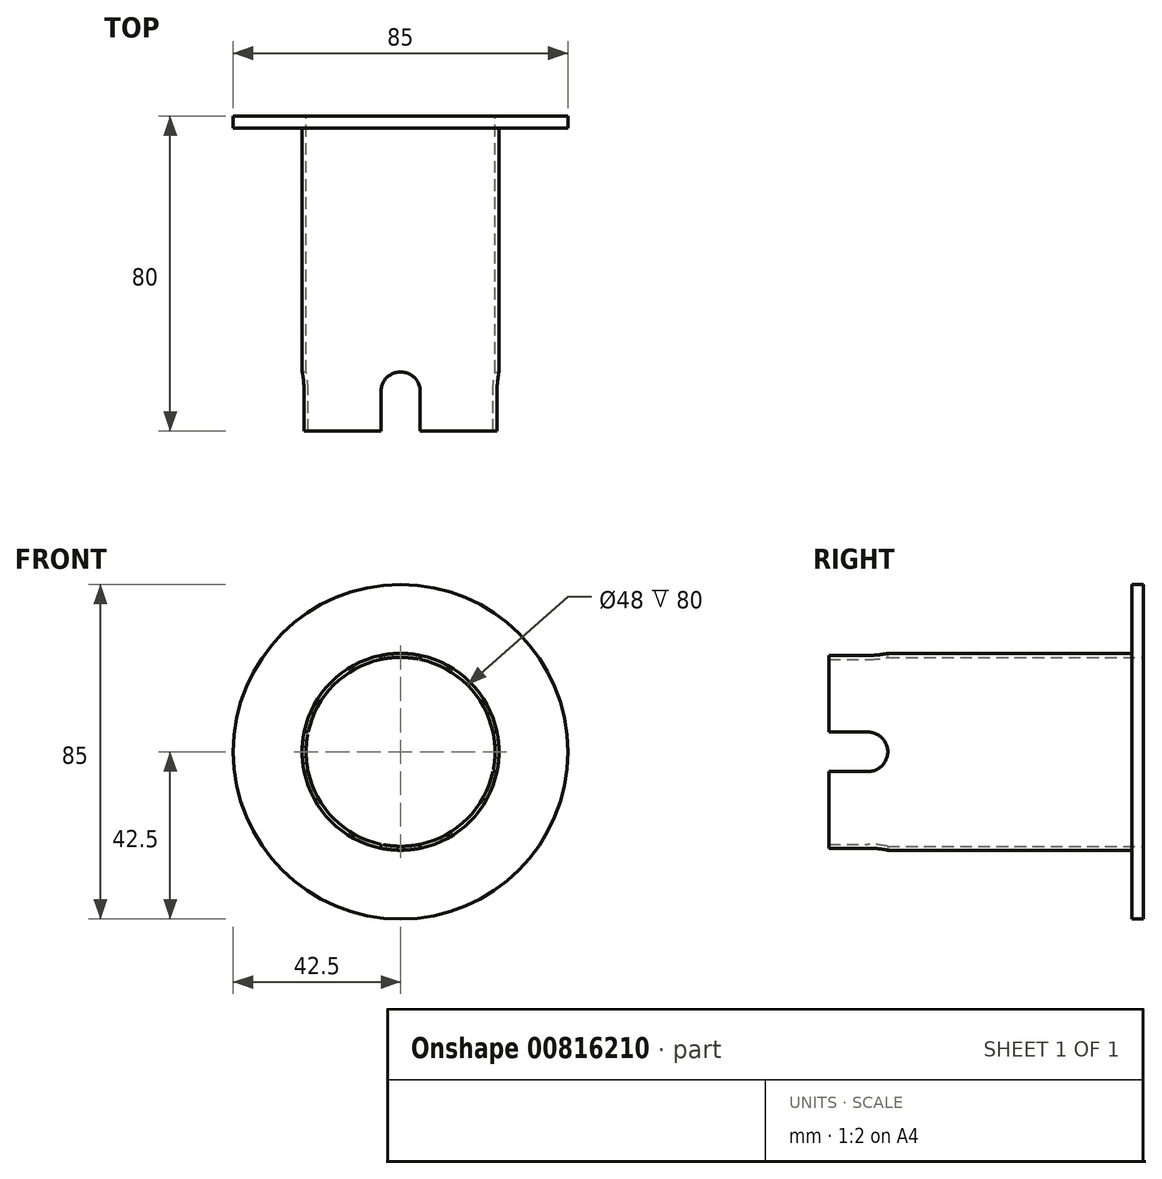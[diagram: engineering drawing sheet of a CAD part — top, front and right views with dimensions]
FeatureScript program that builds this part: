
annotation { "Feature Type Name" : "Feature", "Feature Type Description" : "" }
export const myFeature = defineFeature(function(context is Context, id is Id, definition is map)
    precondition{}
    {
        {
            var Q0;
            Q0=qCreatedBy(makeId("Front.planeOp"),FACE);
            var sketch = newSketch(context, id + "F0", { "sketchPlane" : qUnion([Q0])});
            skCircle(sketch, "E0", {"center": v(0, 0) * mm, "radius": 25 * mm});
            skCircle(sketch, "E1", {"center": v(0, 0) * mm, "radius": 42.5 * mm});
            skCircle(sketch, "E2", {"center": v(0, 0) * mm, "radius": 24 * mm});
            skSolve(sketch);
        }
        {
            var Q0;
            Q0=makeQuery(id+"F0.imprint","IMPRINT",FACE,{"disambiguationData":[TD([[makeQuery(id+"F0.imprint","IMPRINT",EDGE,{"derivedFrom":sQuery(id+"F0.wireOp",EDGE,"E1")}),1.0]])]});
            var Q1;
            Q1=makeQuery(id+"F0.imprint","IMPRINT",FACE,{"disambiguationData":[TD([[makeQuery(id+"F0.imprint","IMPRINT",EDGE,{"derivedFrom":sQuery(id+"F0.wireOp",EDGE,"E0")}),-1.0]])]});
            extrude(context, id + "F1", {"entities" : qUnion([Q0, Q1]), "depth" : 3 * mm, "offsetDistance" : 25 * mm});
        }
        {
            var Q0;
            Q0=qCreatedBy(makeId("Top.planeOp"),FACE);
            cPlane(context, id + "F2", {"entities" : qUnion([Q0]), "cplaneType" : CPlaneType.OFFSET, "offset" : 25 * mm, "width" : 150 * mm, "height" : 150 * mm});
        }
        {
            var Q0;
            Q0=makeQuery(id+"F0.imprint","IMPRINT",FACE,{"disambiguationData":[TD([[makeQuery(id+"F0.imprint","IMPRINT",EDGE,{"derivedFrom":sQuery(id+"F0.wireOp",EDGE,"E0")}),1.0]])]});
            extrude(context, id + "F3", {"entities" : qUnion([Q0]), "operationType" : NewBodyOperationType.ADD, "depth" : 80 * mm, "offsetDistance" : 25 * mm});
        }
        {
            var Q0;
            Q0=qCreatedBy(id+"F2.planeOp",FACE);
            var sketch = newSketch(context, id + "F4", { "sketchPlane" : qUnion([Q0])});
            skLineSegment(sketch, "E3.bottom", {"start": v(-5, -80) * mm, "end": v(5, -80) * mm});
            skLineSegment(sketch, "E3.top", {"start": v(0, -65) * mm, "end": v(0, -65) * mm});
            skLineSegment(sketch, "E3.left", {"start": v(-5, -80) * mm, "end": v(-5, -70) * mm});
            skLineSegment(sketch, "E3.right", {"start": v(5, -80) * mm, "end": v(5, -70) * mm});
            skLineSegment(sketch, "E4", {"start": v(0, -69.84) * mm, "end": v(0, -83.22) * mm, "construction": true});
            skPoint(sketch, "E5", {"position": v(0, -80) * mm});
            skLineSegment(sketch, "E6.0", {"start": v(25, -80) * mm, "end": v(-25, -80) * mm});
            skPoint(sketch, "E7.visualSharp", {"position": v(-5, -65) * mm});
            skArc(sketch, "E7.filletArc", {"start": v(0, -65) * mm, "mid": v(-3.54, -66.46) * mm, "end": v(-5, -70) * mm});
            skPoint(sketch, "E8.visualSharp", {"position": v(5, -65) * mm});
            skArc(sketch, "E8.filletArc", {"start": v(5, -70) * mm, "mid": v(3.54, -66.46) * mm, "end": v(0, -65) * mm});
            skSolve(sketch);
        }
        {
            var Q0;
            {var subQ1=sQuery(id+"F4.wireOp",EDGE,"E3.left");Q0=makeQuery(id+"F4.imprint","IMPRINT",FACE,{"disambiguationData":[TD([[makeQuery(id+"F4.imprint","IMPRINT",EDGE,{"derivedFrom":subQ1}),-1.0]])]});}
            extrude(context, id + "F5", {"entities" : qUnion([Q0]), "oppositeDirection" : true, "depth" : 2 * mm, "offsetDistance" : 25 * mm});
        }
        {
            var Q0;
            Q0=makeQuery(id+"F5.opExtrude","SWEPT_BODY",BODY,{"disambiguationData":[OSD([sQuery(id+"F4.wireOp",EDGE,"E3.left"),sQuery(id+"F4.wireOp",EDGE,"E3.right"),sQuery(id+"F4.wireOp",EDGE,"E6.0"),sQuery(id+"F4.wireOp",EDGE,"E7.filletArc"),sQuery(id+"F4.wireOp",EDGE,"E8.filletArc")])]});
            var Q1;
            Q1=makeQuery(id+"F3.opExtrude","CAP_EDGE",EDGE,{"disambiguationData":[OSD([sQuery(id+"F0.wireOp",EDGE,"E0")])],"isStart":false});
            circularPattern(context, id + "F6", {"operationType" : NewBodyOperationType.REMOVE, "entities" : qUnion([Q0]), "axis" : qUnion([Q1]), "angle" : 360 * degree, "instanceCount" : 4, "equalSpace" : true, "computeTransformsWithoutBuiltin" : true});
        }
        {
            var Q0;
            Q0=makeQuery(id+"F6.boolean.opBoolean","COPY",EDGE,{"derivedFrom":makeQuery(id+"F6.opPattern","COPY",EDGE,{"derivedFrom":makeQuery(id+"F5.opExtrude","SWEPT_EDGE",EDGE,{"disambiguationData":[OSD([sQuery(id+"F4.wireOp",EDGE,"E3.left"),sQuery(id+"F4.wireOp",EDGE,"E6.0")])]}),"instanceName":"2"})});
            var Q1;
            Q1=makeQuery(id+"F6.boolean.opBoolean","COPY",EDGE,{"derivedFrom":makeQuery(id+"F6.opPattern","COPY",EDGE,{"derivedFrom":makeQuery(id+"F5.opExtrude","SWEPT_EDGE",EDGE,{"disambiguationData":[OSD([sQuery(id+"F4.wireOp",EDGE,"E3.right"),sQuery(id+"F4.wireOp",EDGE,"E6.0")])]}),"instanceName":"2"})});
            var Q2;
            Q2=makeQuery(id+"F6.boolean.opBoolean","COPY",EDGE,{"derivedFrom":makeQuery(id+"F6.opPattern","COPY",EDGE,{"derivedFrom":makeQuery(id+"F5.opExtrude","SWEPT_EDGE",EDGE,{"disambiguationData":[OSD([sQuery(id+"F4.wireOp",EDGE,"E3.right"),sQuery(id+"F4.wireOp",EDGE,"E6.0")])]}),"instanceName":"3"})});
            var Q3;
            Q3=makeQuery(id+"F6.boolean.opBoolean","COPY",EDGE,{"derivedFrom":makeQuery(id+"F6.opPattern","COPY",EDGE,{"derivedFrom":makeQuery(id+"F5.opExtrude","SWEPT_EDGE",EDGE,{"disambiguationData":[OSD([sQuery(id+"F4.wireOp",EDGE,"E3.left"),sQuery(id+"F4.wireOp",EDGE,"E6.0")])]}),"instanceName":"3"})});
            var Q4;
            Q4=makeQuery(id+"F6.boolean.opBoolean","COPY",EDGE,{"derivedFrom":makeQuery(id+"F5.opExtrude","SWEPT_EDGE",EDGE,{"disambiguationData":[OSD([sQuery(id+"F4.wireOp",EDGE,"E3.right"),sQuery(id+"F4.wireOp",EDGE,"E6.0")])]})});
            var Q5;
            Q5=makeQuery(id+"F6.boolean.opBoolean","COPY",EDGE,{"derivedFrom":makeQuery(id+"F5.opExtrude","SWEPT_EDGE",EDGE,{"disambiguationData":[OSD([sQuery(id+"F4.wireOp",EDGE,"E3.left"),sQuery(id+"F4.wireOp",EDGE,"E6.0")])]})});
            var Q6;
            Q6=makeQuery(id+"F6.boolean.opBoolean","COPY",EDGE,{"derivedFrom":makeQuery(id+"F6.opPattern","COPY",EDGE,{"derivedFrom":makeQuery(id+"F5.opExtrude","SWEPT_EDGE",EDGE,{"disambiguationData":[OSD([sQuery(id+"F4.wireOp",EDGE,"E3.left"),sQuery(id+"F4.wireOp",EDGE,"E6.0")])]}),"instanceName":"1"})});
            var Q7;
            Q7=makeQuery(id+"F6.boolean.opBoolean","COPY",EDGE,{"derivedFrom":makeQuery(id+"F6.opPattern","COPY",EDGE,{"derivedFrom":makeQuery(id+"F5.opExtrude","SWEPT_EDGE",EDGE,{"disambiguationData":[OSD([sQuery(id+"F4.wireOp",EDGE,"E3.right"),sQuery(id+"F4.wireOp",EDGE,"E6.0")])]}),"instanceName":"1"})});
            fillet(context, id + "F7", {"entities" : qUnion([Q0, Q1, Q2, Q3, Q4, Q5, Q6, Q7]), "radius" : 2 * mm, "tangentPropagation" : true, "allowEdgeOverflow" : false});
        }
    });
